# Revit family: Construction_Roof-Accessories_TRA-Snow-Sun_C21Z-clamp-On
name_source: partatom
category: Specialty Equipment
units: mm (PartAtom-declared; Revit-internal decimal feet)

## family parameters
Classification Number = 23.35.20.31.27.14
Cut with Voids When Loaded = No
Enable Cutting in Views = No
Host = Face
Maintain Annotation Orientation = No
Part Type = Normal
Room Calculation Point = No
Round Connector Dimension = Use Diameter
Shared = No

## types (1)
- C21Z Clamp-on
    Default Elevation = 48 "
    Description = C21Z Clamp-on - Used on: Designed for new construction or retrofit standing seam metal roofs
    Length = 4.38 "
    Manufacturer = TRA Snow & Sun
    Model = C21Z Clamp-on
    Product Documentation Link = https://trasnowandsun.com
    Product Page URL = https://trasnowandsun.com
    Product data url = https://bimobject.com
    URL = https://trasnowandsun.com
    Version = 1
    Weight = 1.35 lbf

## geometry (parser evidence)
native form markers: Sweep x4
no freeform markers — native parametric forms only
